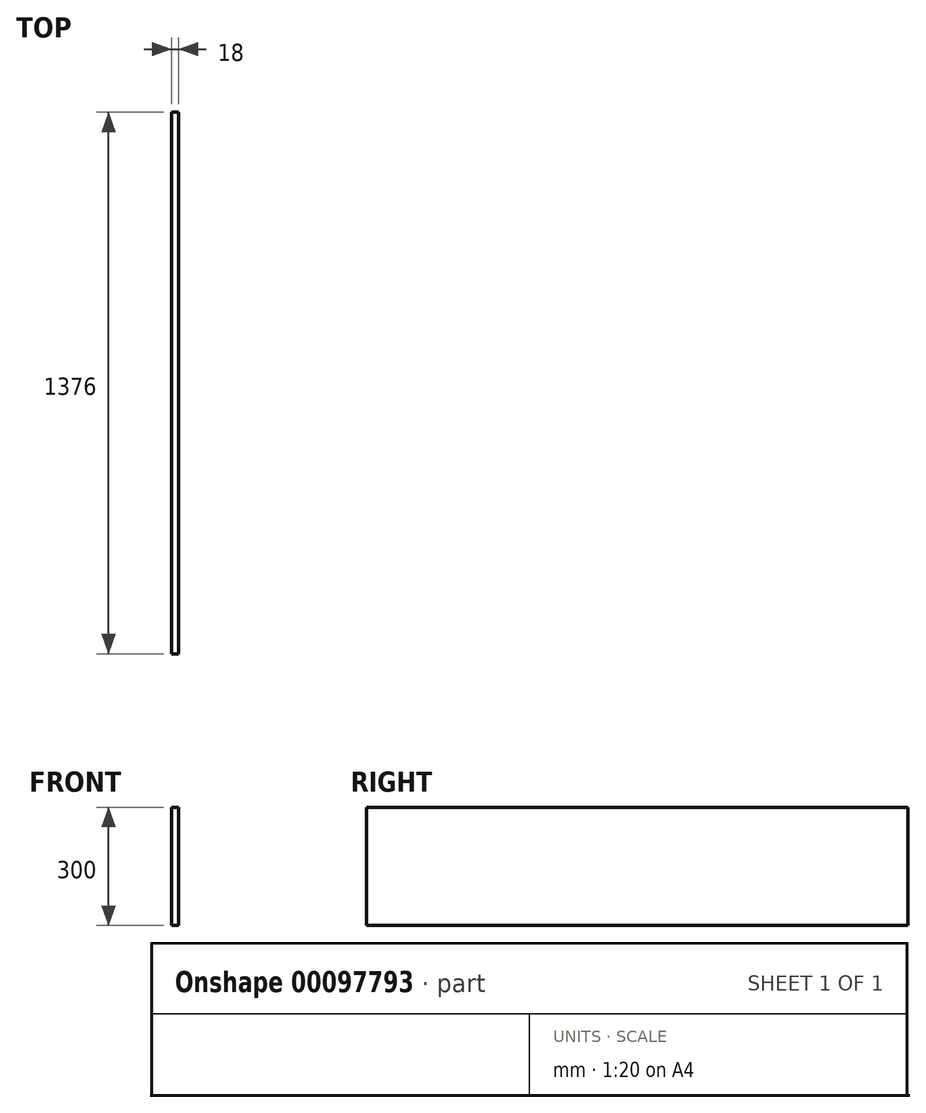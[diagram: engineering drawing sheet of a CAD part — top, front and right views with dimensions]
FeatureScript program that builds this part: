
annotation { "Feature Type Name" : "Feature", "Feature Type Description" : "" }
export const myFeature = defineFeature(function(context is Context, id is Id, definition is map)
    precondition{}
    {
        {
            var Q0;
            Q0=qCreatedBy(makeId("Front.planeOp"),FACE);
            var sketch = newSketch(context, id + "F0", { "sketchPlane" : qUnion([Q0])});
            skLineSegment(sketch, "E0.bottom", {"start": v(0, 0) * mm, "end": v(18, 0) * mm});
            skLineSegment(sketch, "E0.top", {"start": v(0, 300) * mm, "end": v(18, 300) * mm});
            skLineSegment(sketch, "E0.left", {"start": v(0, 0) * mm, "end": v(0, 300) * mm});
            skLineSegment(sketch, "E0.right", {"start": v(18, 0) * mm, "end": v(18, 300) * mm});
            skSolve(sketch);
        }
        {
            var Q0;
            Q0=qSketchRegion(id+"F0",true);
            extrude(context, id + "F1", {"entities" : qUnion([Q0]), "oppositeDirection" : true, "depth" : 1376 * mm});
        }
    });
